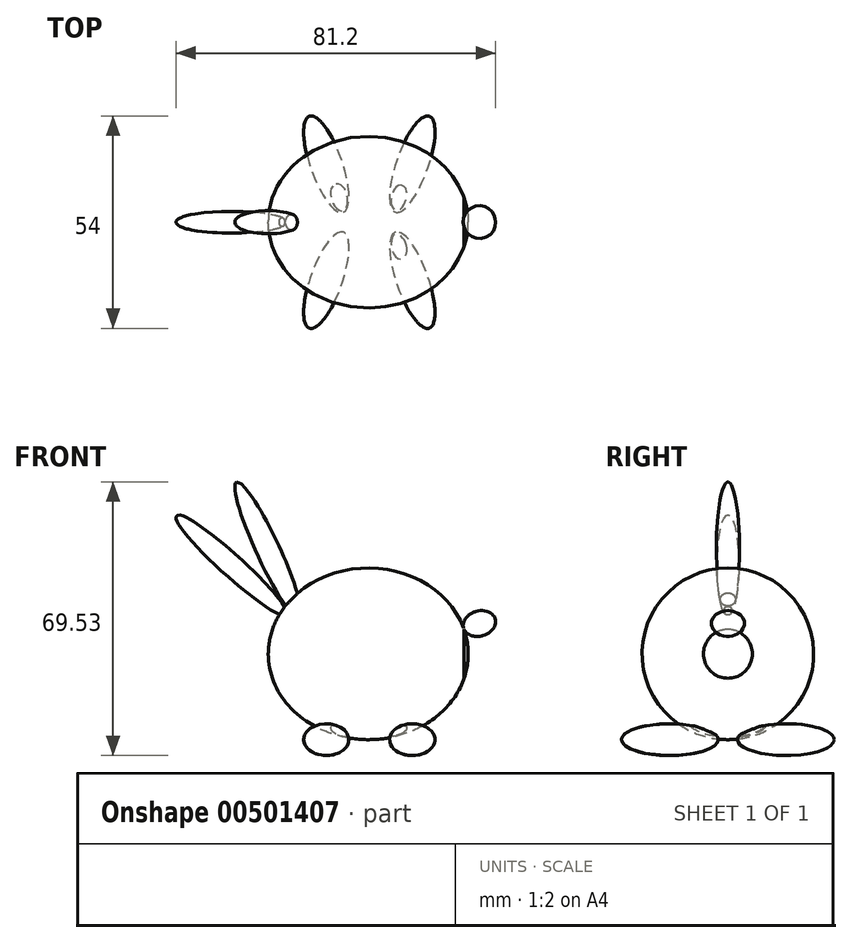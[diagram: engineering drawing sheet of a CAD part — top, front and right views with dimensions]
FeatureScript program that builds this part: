
annotation { "Feature Type Name" : "Feature", "Feature Type Description" : "" }
export const myFeature = defineFeature(function(context is Context, id is Id, definition is map)
    precondition{}
    {
        {
            var Q0;
            Q0=qCreatedBy(makeId("Front.planeOp"),FACE);
            var sketch = newSketch(context, id + "F0", { "sketchPlane" : qUnion([Q0])});
            skEllipticalArc(sketch, "E0", {});
            skEllipticalArc(sketch, "E1", {});
            skEllipticalArc(sketch, "E2", {});
            skArc(sketch, "E3", {"start": v(-32.43, 64.9) * mm, "mid": v(-32.54, 65) * mm, "end": v(-32.67, 65.08) * mm});
            skEllipticalArc(sketch, "E4.trimOffspring", {});
            skEllipticalArc(sketch, "E5.trimOffspring", {});
            skEllipticalArc(sketch, "E6", {});
            skLineSegment(sketch, "E7", {"start": v(-25.67, 21.8) * mm, "end": v(25.13, 21.8) * mm});
            skLineSegment(sketch, "E8", {"start": v(27.1, 32.58) * mm, "end": v(28.86, 26.44) * mm});
            skPoint(sketch, "E9", {"position": v(0, 0) * mm});
            skPoint(sketch, "E10", {"position": v(0, 43.6) * mm});
            skPoint(sketch, "E10.positionSnap0", {"position": v(-0.27, 43.6) * mm});
            skPoint(sketch, "E11", {"position": v(24.08, 28) * mm});
            skLineSegment(sketch, "E12", {"start": v(-48.98, 56.91) * mm, "end": v(-22.23, 32.75) * mm});
            skPoint(sketch, "E12.startSnap0", {"position": v(-48.98, 56.78) * mm});
            skPoint(sketch, "E13.positionSnap0", {"position": v(-33.74, 65.43) * mm});
            skLineSegment(sketch, "E14", {"start": v(-33.74, 65.43) * mm, "end": v(-19.91, 35.62) * mm});
            skLineSegment(sketch, "E15", {"start": v(23.93, 28.41) * mm, "end": v(24.08, 28) * mm});
            const initialGuessF0  = {"E0": [-0.0002706010891221959, 0.021800935703122082, -1, 0, 0.0254, 0.021802172999542516, 3.4496317782555095, 3.430024824577874], "E1": [-0.03477020512528624, 0.04408406480151432, 0.745761206908761, -0.666213345911044, 0.01905, 0.0027591740995862096, 3.0450619344628835, 5.824511886912878], "E2": [-0.025729684503843886, 0.04814716565868875, 0.4204609624606676, -0.9073106298543235, 0.01905, 0.002941751105215147, 2.8569508533475814, 5.590013378925223], "E4.trimOffspring": [-0.03477020512528624, 0.04408406480151432, 0.745761206908761, -0.666213345911044, 0.01905, 0.0027591740995862096, 0.49589126009521334, 3.0450619344628826], "E5.trimOffspring": [-0.025729684503843886, 0.04814716565868875, 0.4204609624606676, -0.9073106298543235, 0.01905, 0.002941751105215147, 0.8132786182350754, 2.8099183082722985], "E6": [0.02797813968025131, 0.029507293664743427, -0.961523918287649, -0.2747212306334669, 0.004190514139188014, 0.0031948029281469435, 0.11795940255709228, 6.265313776215399]};
            skSetInitialGuess(sketch, initialGuessF0);
            skSolve(sketch);
        }
        {
            var Q0;
            {var subQ5=sQuery(id+"F0.wireOp",EDGE,"E7");Q0=makeQuery(id+"F0.imprint","IMPRINT",FACE,{"disambiguationData":[TD([[makeQuery(id+"F0.imprint","IMPRINT",EDGE,{"derivedFrom":subQ5}),1.0]])]});}
            var Q1;
            Q1=sQuery(id+"F0.wireOp",EDGE,"E7");
            revolve(context, id + "F1", {"entities" : qUnion([Q0]), "axis" : qUnion([Q1]), "revolveType" : RevolveType.FULL});
        }
        {
            var Q0;
            {var subQ0=sQuery(id+"F0.wireOp",EDGE,"E8");Q0=makeQuery(id+"F0.imprint","IMPRINT",FACE,{"disambiguationData":[TD([[makeQuery(id+"F0.imprint","IMPRINT",EDGE,{"derivedFrom":subQ0}),1.0]])]});}
            var Q1;
            Q1=sQuery(id+"F0.wireOp",EDGE,"E8");
            revolve(context, id + "F2", {"entities" : qUnion([Q0]), "axis" : qUnion([Q1]), "revolveType" : RevolveType.FULL});
        }
        {
            var Q0;
            Q0=qCreatedBy(makeId("Top.planeOp"),FACE);
            var sketch = newSketch(context, id + "F3", { "sketchPlane" : qUnion([Q0])});
            skEllipse(sketch, "E16", {"center": v(-10.92, -14.73) * mm, "majorRadius": 12.93 * mm, "minorRadius": 4.05 * mm, "majorAxis": v(0.33, 0.94)});
            skEllipse(sketch, "E17.MirrorC", {"center": v(10.92, -14.73) * mm, "majorRadius": 12.93 * mm, "minorRadius": 4.05 * mm, "majorAxis": v(-0.33, 0.94)});
            skPoint(sketch, "E18", {"position": v(-15.24, -26.92) * mm});
            skPoint(sketch, "E18.positionSnap0", {"position": v(-15.24, -26.92) * mm});
            skPoint(sketch, "E19", {"position": v(15.24, -26.92) * mm});
            skPoint(sketch, "E19.positionSnap0", {"position": v(15.24, -26.92) * mm});
            skPoint(sketch, "E20", {"position": v(6.6, -2.54) * mm});
            skPoint(sketch, "E20.positionSnap0", {"position": v(6.6, -2.54) * mm});
            skPoint(sketch, "E21", {"position": v(-6.6, -2.54) * mm});
            skPoint(sketch, "E21.positionSnap0", {"position": v(-6.6, -2.54) * mm});
            skLineSegment(sketch, "E22", {"start": v(-15.24, -26.92) * mm, "end": v(-6.6, -2.54) * mm});
            skLineSegment(sketch, "E23.MirrorCS", {"start": v(15.24, -26.92) * mm, "end": v(6.6, -2.54) * mm});
            skEllipse(sketch, "E24.MirrorC", {"center": v(10.92, 14.73) * mm, "majorRadius": 12.93 * mm, "minorRadius": 4.05 * mm, "majorAxis": v(-0.33, -0.94)});
            skLineSegment(sketch, "E25.MirrorCS", {"start": v(15.24, 26.92) * mm, "end": v(6.6, 2.54) * mm});
            skEllipse(sketch, "E26.MirrorC", {"center": v(-10.92, 14.73) * mm, "majorRadius": 12.93 * mm, "minorRadius": 4.05 * mm, "majorAxis": v(0.33, -0.94)});
            skLineSegment(sketch, "E27.MirrorCS", {"start": v(-15.24, 26.92) * mm, "end": v(-6.6, 2.54) * mm});
            skSolve(sketch);
        }
        {
            var Q0;
            {var subQ0=sQuery(id+"F3.wireOp",EDGE,"E22");Q0=makeQuery(id+"F3.imprint","IMPRINT",FACE,{"disambiguationData":[TD([[makeQuery(id+"F3.imprint","IMPRINT",EDGE,{"derivedFrom":subQ0}),1.0]])]});}
            var Q1;
            Q1=sQuery(id+"F3.wireOp",EDGE,"E22");
            revolve(context, id + "F4", {"entities" : qUnion([Q0]), "axis" : qUnion([Q1]), "revolveType" : RevolveType.FULL});
        }
        {
            var Q0;
            {var subQ0=sQuery(id+"F3.wireOp",EDGE,"E23.MirrorCS");Q0=makeQuery(id+"F3.imprint","IMPRINT",FACE,{"disambiguationData":[TD([[makeQuery(id+"F3.imprint","IMPRINT",EDGE,{"derivedFrom":subQ0}),-1.0]])]});}
            var Q1;
            Q1=sQuery(id+"F3.wireOp",EDGE,"E23.MirrorCS");
            revolve(context, id + "F5", {"operationType" : NewBodyOperationType.ADD, "entities" : qUnion([Q0]), "axis" : qUnion([Q1]), "revolveType" : RevolveType.FULL});
        }
        {
            var Q0;
            {var subQ0=sQuery(id+"F3.wireOp",EDGE,"E25.MirrorCS");Q0=makeQuery(id+"F3.imprint","IMPRINT",FACE,{"disambiguationData":[TD([[makeQuery(id+"F3.imprint","IMPRINT",EDGE,{"derivedFrom":subQ0}),-1.0]])]});}
            var Q1;
            Q1=sQuery(id+"F3.wireOp",EDGE,"E25.MirrorCS");
            revolve(context, id + "F6", {"operationType" : NewBodyOperationType.ADD, "entities" : qUnion([Q0]), "axis" : qUnion([Q1]), "revolveType" : RevolveType.FULL});
        }
        {
            var Q0;
            {var subQ0=sQuery(id+"F3.wireOp",EDGE,"E27.MirrorCS");Q0=makeQuery(id+"F3.imprint","IMPRINT",FACE,{"disambiguationData":[TD([[makeQuery(id+"F3.imprint","IMPRINT",EDGE,{"derivedFrom":subQ0}),-1.0]])]});}
            var Q1;
            Q1=sQuery(id+"F3.wireOp",EDGE,"E27.MirrorCS");
            revolve(context, id + "F7", {"operationType" : NewBodyOperationType.ADD, "entities" : qUnion([Q0]), "axis" : qUnion([Q1]), "revolveType" : RevolveType.FULL});
        }
        {
            var Q0;
            {var subQ0=sQuery(id+"F0.wireOp",EDGE,"E1");var subQ1=sQuery(id+"F0.wireOp",EDGE,"E0");var subQ2=makeQuery(id+"F0.imprint","INTERSECT",VERTEX,{"derivedFrom":[subQ1,subQ0]});Q0=makeQuery(id+"F0.imprint","IMPRINT",FACE,{"disambiguationData":[TD([[makeQuery(id+"F0.imprint","IMPRINT",EDGE,{"disambiguationData":[TD([[subQ2,1.0]])],"derivedFrom":subQ1}),-1.0]])]});}
            var Q1;
            Q1=sQuery(id+"F0.wireOp",EDGE,"E12");
            revolve(context, id + "F8", {"operationType" : NewBodyOperationType.ADD, "entities" : qUnion([Q0]), "axis" : qUnion([Q1]), "revolveType" : RevolveType.FULL});
        }
        {
            var Q0;
            {var subQ3=sQuery(id+"F0.wireOp",EDGE,"E14");Q0=makeQuery(id+"F0.imprint","IMPRINT",FACE,{"disambiguationData":[TD([[makeQuery(id+"F0.imprint","IMPRINT",EDGE,{"derivedFrom":subQ3}),-1.0]])]});}
            var Q1;
            Q1=sQuery(id+"F0.wireOp",EDGE,"E14");
            revolve(context, id + "F9", {"operationType" : NewBodyOperationType.ADD, "entities" : qUnion([Q0]), "axis" : qUnion([Q1]), "revolveType" : RevolveType.FULL});
        }
    });
